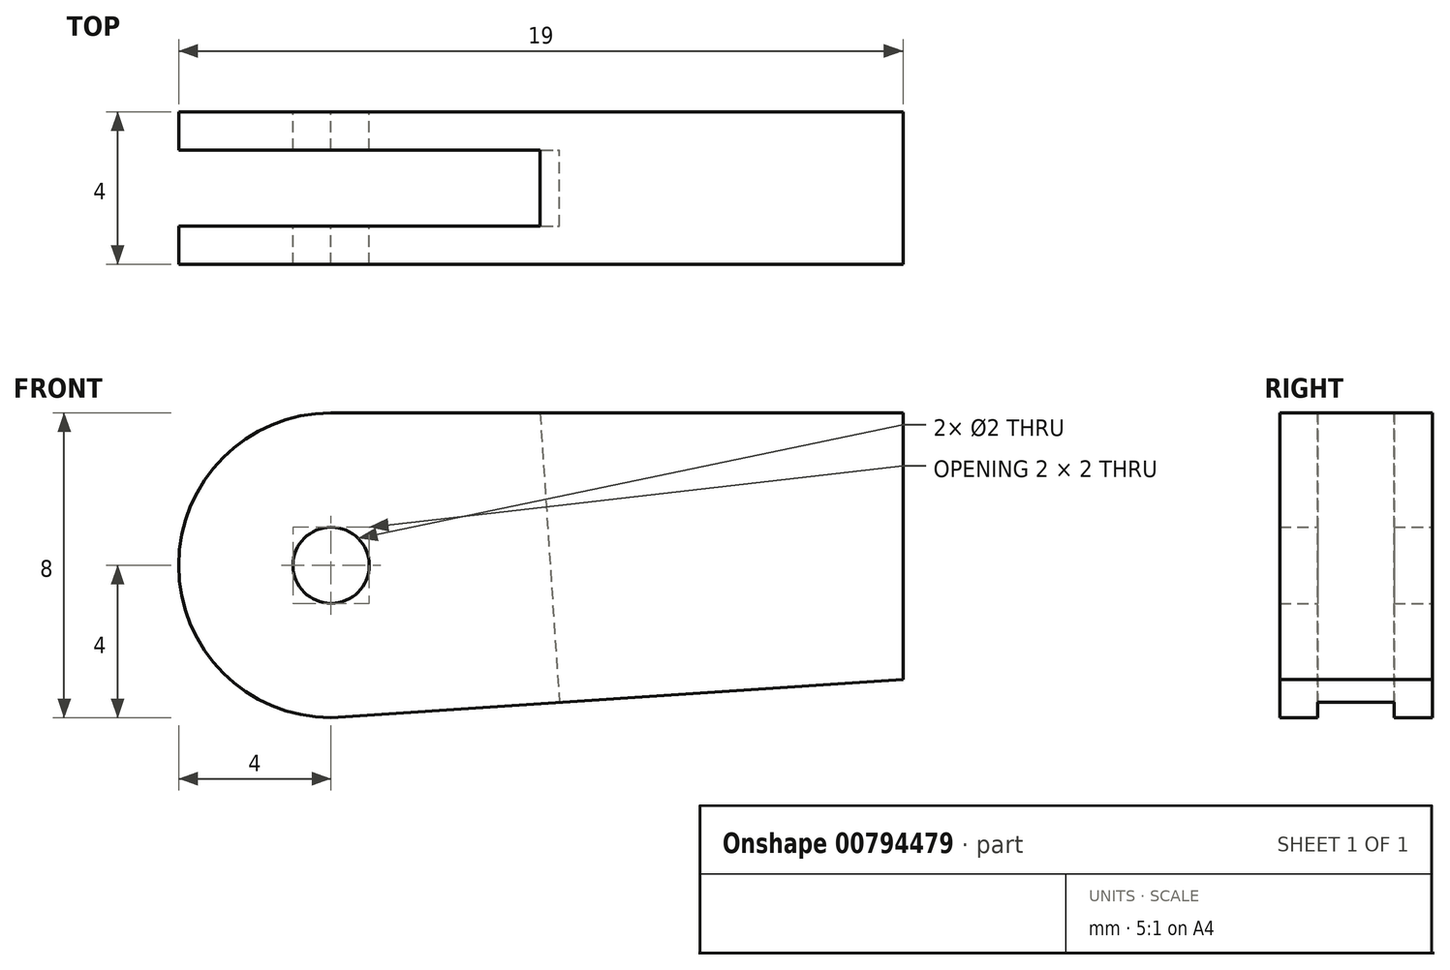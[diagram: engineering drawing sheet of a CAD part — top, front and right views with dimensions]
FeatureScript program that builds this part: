
annotation { "Feature Type Name" : "Feature", "Feature Type Description" : "" }
export const myFeature = defineFeature(function(context is Context, id is Id, definition is map)
    precondition{}
    {
        {
            var Q0;
            Q0=qCreatedBy(makeId("Front.planeOp"),FACE);
            var sketch = newSketch(context, id + "F0", { "sketchPlane" : qUnion([Q0])});
            skCircle(sketch, "E0", {"center": v(0, 4) * mm, "radius": 1 * mm});
            skArc(sketch, "E1", {"start": v(0, 8) * mm, "mid": v(-4, 4) * mm, "end": v(0, 0) * mm});
            skLineSegment(sketch, "E2", {"start": v(0, 0) * mm, "end": v(15, 1) * mm});
            skLineSegment(sketch, "E3", {"start": v(15, 1) * mm, "end": v(15, 8) * mm});
            skLineSegment(sketch, "E4", {"start": v(0, 8) * mm, "end": v(15, 8) * mm});
            skSolve(sketch);
        }
        {
            var Q0;
            Q0=makeQuery(id+"F0.imprint","IMPRINT",FACE,{"disambiguationData":[TD([[makeQuery(id+"F0.imprint","IMPRINT",EDGE,{"derivedFrom":sQuery(id+"F0.wireOp",EDGE,"E0")}),-1.0]])]});
            extrude(context, id + "F1", {"entities" : qUnion([Q0]), "depth" : 4 * mm, "offsetDistance" : 25 * mm});
        }
        {
            var Q0;
            Q0=makeQuery(id+"F1.opExtrude","SWEPT_FACE",FACE,{"disambiguationData":[OSD([sQuery(id+"F0.wireOp",EDGE,"E2")])]});
            var sketch = newSketch(context, id + "F2", { "sketchPlane" : qUnion([Q0])});
            skLineSegment(sketch, "E5", {"start": v(0, 2) * mm, "end": v(0, 2) * mm});
            skLineSegment(sketch, "E6", {"start": v(0, 2) * mm, "end": v(-10.38, 2) * mm, "construction": true});
            skLineSegment(sketch, "E7.bottom", {"start": v(-6, 3) * mm, "end": v(6, 3) * mm});
            skLineSegment(sketch, "E7.top", {"start": v(-6, 1) * mm, "end": v(6, 1) * mm});
            skLineSegment(sketch, "E7.left", {"start": v(-6, 3) * mm, "end": v(-6, 1) * mm});
            skLineSegment(sketch, "E7.right", {"start": v(6, 3) * mm, "end": v(6, 1) * mm});
            skPoint(sketch, "E7.middle", {"position": v(0, 2) * mm});
            skSolve(sketch);
        }
        {
            var Q0;
            Q0 = qSketchRegion(id + "F2", true);
            extrude(context, id + "F3", {"entities" : qUnion([Q0]), "operationType" : NewBodyOperationType.REMOVE, "endBound" : BoundingType.THROUGH_ALL, "oppositeDirection" : true, "depth" : 25 * mm, "offsetDistance" : 25 * mm});
        }
    });
